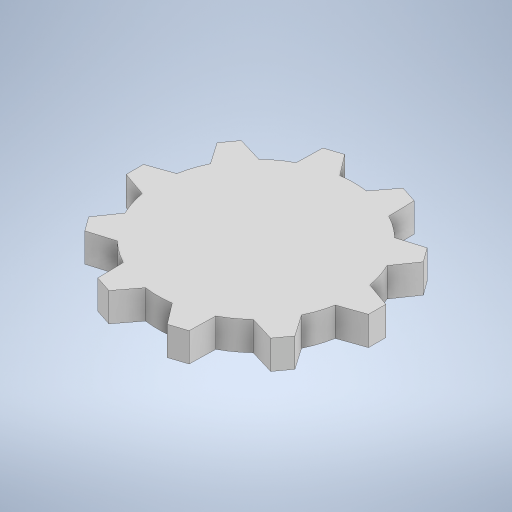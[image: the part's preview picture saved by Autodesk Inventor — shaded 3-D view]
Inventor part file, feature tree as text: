
AUTODESK INVENTOR PART (.ipt)
format: ipt  version: 2024 (Build 280153000, 153)  size: 272,384 bytes
history: native  units: in
note: dims shown in document units (in); Inventor stores cm internally (conversion verified against a paired STEP export)
features: extrude x1
ambient origin geometry x8: Origin, YZ Plane, XZ Plane, XY Plane, X Axis, Y Axis, Z Axis, Center Point
bodies: Solid1 (feature_tree)
feature tree (1):
  extrude  "Extrusion1"  Depth=1.3386in
